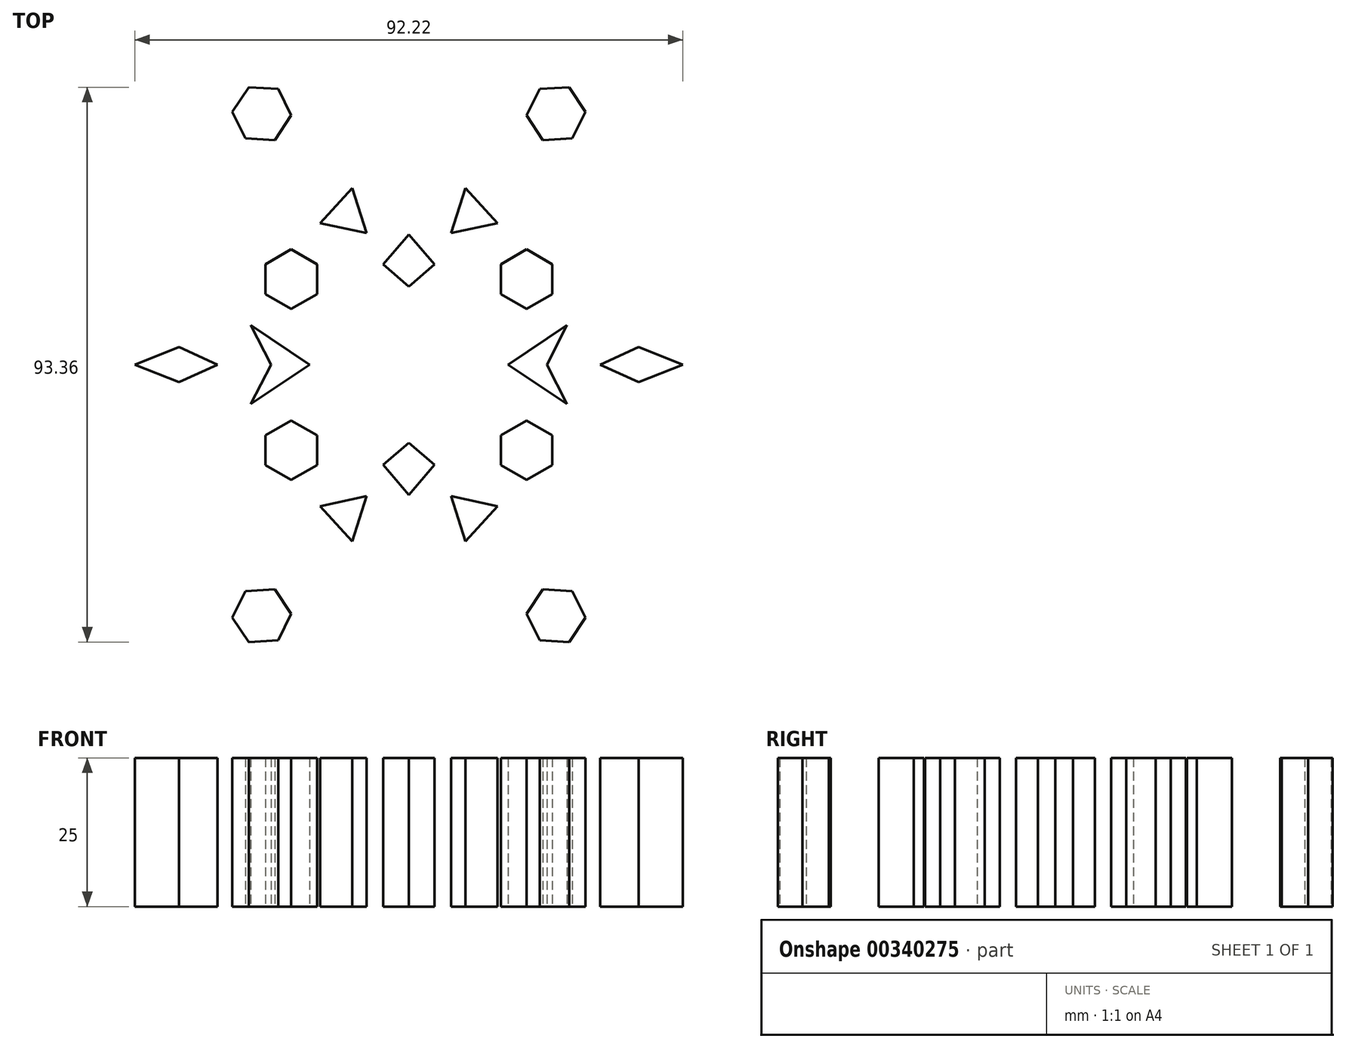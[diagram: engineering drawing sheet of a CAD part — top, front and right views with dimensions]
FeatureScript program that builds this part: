
annotation { "Feature Type Name" : "Feature", "Feature Type Description" : "" }
export const myFeature = defineFeature(function(context is Context, id is Id, definition is map)
    precondition{}
    {
        {
            var Q0;
            Q0=qCreatedBy(makeId("Top.planeOp"),FACE);
            var sketch = newSketch(context, id + "F0", { "sketchPlane" : qUnion([Q0])});
            skLineSegment(sketch, "E0.0", {"start": v(-31.3, 54.1) * mm, "end": v(31.2, 54.15) * mm});
            skLineSegment(sketch, "E0.1", {"start": v(31.2, 54.15) * mm, "end": v(62.5, 0.05) * mm});
            skLineSegment(sketch, "E0.2", {"start": v(62.5, 0.05) * mm, "end": v(31.3, -54.1) * mm});
            skLineSegment(sketch, "E0.3", {"start": v(31.3, -54.1) * mm, "end": v(-31.2, -54.15) * mm});
            skLineSegment(sketch, "E0.4", {"start": v(-31.2, -54.15) * mm, "end": v(-62.5, -0.05) * mm});
            skLineSegment(sketch, "E0.5", {"start": v(-62.5, -0.05) * mm, "end": v(-31.3, 54.1) * mm});
            skLineSegment(sketch, "E1.0", {"start": v(-37.55, 13.07) * mm, "end": v(-54.8, 12.82) * mm});
            skLineSegment(sketch, "E1.4", {"start": v(-39, 41.23) * mm, "end": v(-30.16, 26.43) * mm});
            skLineSegment(sketch, "E1.5", {"start": v(-30.16, 26.43) * mm, "end": v(-37.55, 13.07) * mm});
            skLineSegment(sketch, "E2.MirrorCS", {"start": v(39, 41.23) * mm, "end": v(30.16, 26.43) * mm});
            skLineSegment(sketch, "E3.MirrorCS", {"start": v(30.16, 26.43) * mm, "end": v(37.55, 13.07) * mm});
            skLineSegment(sketch, "E4.MirrorCS", {"start": v(37.55, 13.07) * mm, "end": v(54.8, 12.82) * mm});
            skLineSegment(sketch, "E5.MirrorCS", {"start": v(-37.55, -13.07) * mm, "end": v(-54.8, -12.82) * mm});
            skLineSegment(sketch, "E6.MirrorCS", {"start": v(-30.16, -26.43) * mm, "end": v(-37.55, -13.07) * mm});
            skLineSegment(sketch, "E7.MirrorCS", {"start": v(-39, -41.23) * mm, "end": v(-30.16, -26.43) * mm});
            skLineSegment(sketch, "E8.MirrorCS", {"start": v(39, -41.23) * mm, "end": v(30.16, -26.43) * mm});
            skLineSegment(sketch, "E9.MirrorCS", {"start": v(30.16, -26.43) * mm, "end": v(37.55, -13.07) * mm});
            skLineSegment(sketch, "E10.MirrorCS", {"start": v(37.55, -13.07) * mm, "end": v(54.8, -12.82) * mm});
            skLineSegment(sketch, "E11.0", {"start": v(-8.68, 41.12) * mm, "end": v(-16.3, 54.12) * mm});
            skLineSegment(sketch, "E11.4", {"start": v(16.2, 53.88) * mm, "end": v(6.98, 40.87) * mm});
            skLineSegment(sketch, "E11.5", {"start": v(6.98, 40.87) * mm, "end": v(-8.68, 41.12) * mm});
            skLineSegment(sketch, "E12.MirrorCS", {"start": v(-8.68, -41.12) * mm, "end": v(-16.3, -54.12) * mm});
            skLineSegment(sketch, "E13.MirrorCS", {"start": v(6.98, -40.87) * mm, "end": v(-8.68, -41.12) * mm});
            skLineSegment(sketch, "E14.MirrorCS", {"start": v(16.2, -53.88) * mm, "end": v(6.98, -40.87) * mm});
            skLineSegment(sketch, "E15.0", {"start": v(-7.43, 4.18) * mm, "end": v(-0.1, 8.52) * mm});
            skLineSegment(sketch, "E15.1", {"start": v(-0.1, 8.52) * mm, "end": v(7.33, 4.34) * mm});
            skLineSegment(sketch, "E15.2", {"start": v(7.33, 4.34) * mm, "end": v(7.43, -4.18) * mm});
            skLineSegment(sketch, "E15.3", {"start": v(7.43, -4.18) * mm, "end": v(0.1, -8.52) * mm});
            skLineSegment(sketch, "E15.4", {"start": v(0.1, -8.52) * mm, "end": v(-7.33, -4.34) * mm});
            skLineSegment(sketch, "E15.5", {"start": v(-7.33, -4.34) * mm, "end": v(-7.43, 4.18) * mm});
            skSolve(sketch);
        }
        {
            var Q0;
            {var subQ5=sQuery(id+"F0.wireOp",EDGE,"E0.3");Q0=makeQuery(id+"F0.imprint","IMPRINT",FACE,{"disambiguationData":[TD([[makeQuery(id+"F0.imprint","IMPRINT",EDGE,{"derivedFrom":subQ5}),-1.0]])]});}
            var sketch = newSketch(context, id + "F1", { "sketchPlane" : qUnion([Q0])});
            skLineSegment(sketch, "E16", {"start": v(-49.5, 13.15) * mm, "end": v(-41.77, 5.72) * mm});
            skLineSegment(sketch, "E17", {"start": v(-41.77, 5.72) * mm, "end": v(-45.64, 14.08) * mm});
            skPoint(sketch, "E17.endSnap0", {"position": v(-45.64, 9.44) * mm});
            skLineSegment(sketch, "E18", {"start": v(-37.75, 13.15) * mm, "end": v(-34.84, 6.87) * mm});
            skLineSegment(sketch, "E19", {"start": v(-34.84, 6.87) * mm, "end": v(-34.84, 18.41) * mm});
            skLineSegment(sketch, "E20", {"start": v(-34.84, 18.41) * mm, "end": v(-26, 23.36) * mm});
            skLineSegment(sketch, "E21", {"start": v(-26, 23.36) * mm, "end": v(-31.25, 26.77) * mm});
            skLineSegment(sketch, "E22", {"start": v(-58.8, 6.34) * mm, "end": v(-52.3, 3.25) * mm});
            skLineSegment(sketch, "E23", {"start": v(-52.3, 3.25) * mm, "end": v(-56.94, 10.06) * mm});
            skLineSegment(sketch, "E24", {"start": v(-31.25, 26.77) * mm, "end": v(-23.2, 26.77) * mm});
            skLineSegment(sketch, "E25", {"start": v(-23.2, 26.77) * mm, "end": v(-34.66, 32.95) * mm});
            skLineSegment(sketch, "E26", {"start": v(-12.07, 46.57) * mm, "end": v(-12.07, 32.95) * mm});
            skLineSegment(sketch, "E27", {"start": v(-12.07, 32.95) * mm, "end": v(-8.66, 39.76) * mm});
            skPoint(sketch, "E27.endSnap0", {"position": v(-12.07, 39.76) * mm});
            skLineSegment(sketch, "E28", {"start": v(-8.66, 39.76) * mm, "end": v(0, 35.43) * mm});
            skCircle(sketch, "E29.cCircle", {"center": v(-24.75, 42.24) * mm, "radius": 4.96 * mm, "construction": true});
            skLineSegment(sketch, "E29.0", {"start": v(-19.8, 41.93) * mm, "end": v(-22.55, 37.8) * mm});
            skLineSegment(sketch, "E29.1", {"start": v(-22.55, 37.8) * mm, "end": v(-27.5, 38.1) * mm});
            skLineSegment(sketch, "E29.2", {"start": v(-27.5, 38.1) * mm, "end": v(-29.7, 42.55) * mm});
            skLineSegment(sketch, "E29.3", {"start": v(-29.7, 42.55) * mm, "end": v(-26.96, 46.68) * mm});
            skLineSegment(sketch, "E29.4", {"start": v(-26.96, 46.68) * mm, "end": v(-22.01, 46.37) * mm});
            skLineSegment(sketch, "E29.5", {"start": v(-22.01, 46.37) * mm, "end": v(-19.8, 41.93) * mm});
            skLineSegment(sketch, "E30.MirrorCS", {"start": v(8.66, 39.76) * mm, "end": v(0, 35.43) * mm});
            skLineSegment(sketch, "E31.MirrorCS", {"start": v(12.07, 32.95) * mm, "end": v(8.66, 39.76) * mm});
            skPoint(sketch, "E32.MirrorP", {"position": v(12.07, 39.76) * mm});
            skLineSegment(sketch, "E33.MirrorCS", {"start": v(12.07, 46.57) * mm, "end": v(12.07, 32.95) * mm});
            skLineSegment(sketch, "E34.MirrorCS", {"start": v(23.2, 26.77) * mm, "end": v(34.66, 32.95) * mm});
            skLineSegment(sketch, "E35.MirrorCS", {"start": v(31.25, 26.77) * mm, "end": v(23.2, 26.77) * mm});
            skLineSegment(sketch, "E36.MirrorCS", {"start": v(34.84, 18.41) * mm, "end": v(26, 23.36) * mm});
            skLineSegment(sketch, "E37.MirrorCS", {"start": v(26, 23.36) * mm, "end": v(31.25, 26.77) * mm});
            skLineSegment(sketch, "E38.MirrorCS", {"start": v(34.84, 6.87) * mm, "end": v(34.84, 18.41) * mm});
            skPoint(sketch, "E39.MirrorP", {"position": v(45.64, 9.44) * mm});
            skLineSegment(sketch, "E40.MirrorCS", {"start": v(37.75, 13.15) * mm, "end": v(34.84, 6.87) * mm});
            skLineSegment(sketch, "E41.MirrorCS", {"start": v(41.77, 5.72) * mm, "end": v(45.64, 14.08) * mm});
            skLineSegment(sketch, "E42.MirrorCS", {"start": v(49.5, 13.15) * mm, "end": v(41.77, 5.72) * mm});
            skLineSegment(sketch, "E43.MirrorCS", {"start": v(58.8, 6.34) * mm, "end": v(52.3, 3.25) * mm});
            skLineSegment(sketch, "E44.MirrorCS", {"start": v(52.3, 3.25) * mm, "end": v(56.94, 10.06) * mm});
            skLineSegment(sketch, "E45.MirrorCS", {"start": v(41.77, -5.72) * mm, "end": v(45.64, -14.08) * mm});
            skLineSegment(sketch, "E46.MirrorCS", {"start": v(49.5, -13.15) * mm, "end": v(41.77, -5.72) * mm});
            skPoint(sketch, "E47.MirrorP", {"position": v(45.64, -9.44) * mm});
            skLineSegment(sketch, "E48.MirrorCS", {"start": v(-22.55, -37.8) * mm, "end": v(-27.5, -38.1) * mm});
            skLineSegment(sketch, "E49.MirrorCS", {"start": v(-22.01, -46.37) * mm, "end": v(-19.8, -41.93) * mm});
            skLineSegment(sketch, "E50.MirrorCS", {"start": v(26, -23.36) * mm, "end": v(31.25, -26.77) * mm});
            skCircle(sketch, "E51.MirrorC", {"center": v(-24.75, -42.24) * mm, "radius": 4.96 * mm, "construction": true});
            skLineSegment(sketch, "E52.MirrorCS", {"start": v(37.75, -13.15) * mm, "end": v(34.84, -6.87) * mm});
            skLineSegment(sketch, "E53.MirrorCS", {"start": v(-19.8, -41.93) * mm, "end": v(-22.55, -37.8) * mm});
            skLineSegment(sketch, "E54.MirrorCS", {"start": v(-12.07, -32.95) * mm, "end": v(-8.66, -39.76) * mm});
            skLineSegment(sketch, "E55.MirrorCS", {"start": v(31.25, -26.77) * mm, "end": v(23.2, -26.77) * mm});
            skLineSegment(sketch, "E56.MirrorCS", {"start": v(-26.96, -46.68) * mm, "end": v(-22.01, -46.37) * mm});
            skLineSegment(sketch, "E57.MirrorCS", {"start": v(-27.5, -38.1) * mm, "end": v(-29.7, -42.55) * mm});
            skLineSegment(sketch, "E58.MirrorCS", {"start": v(-31.25, -26.77) * mm, "end": v(-23.2, -26.77) * mm});
            skLineSegment(sketch, "E59.MirrorCS", {"start": v(-29.7, -42.55) * mm, "end": v(-26.96, -46.68) * mm});
            skLineSegment(sketch, "E60.MirrorCS", {"start": v(12.07, -32.95) * mm, "end": v(8.66, -39.76) * mm});
            skLineSegment(sketch, "E61.MirrorCS", {"start": v(-26, -23.36) * mm, "end": v(-31.25, -26.77) * mm});
            skLineSegment(sketch, "E62.MirrorCS", {"start": v(-37.75, -13.15) * mm, "end": v(-34.84, -6.87) * mm});
            skLineSegment(sketch, "E63.MirrorCS", {"start": v(34.84, -6.87) * mm, "end": v(34.84, -18.41) * mm});
            skLineSegment(sketch, "E64.MirrorCS", {"start": v(-49.5, -13.15) * mm, "end": v(-41.77, -5.72) * mm});
            skLineSegment(sketch, "E65.MirrorCS", {"start": v(-58.8, -6.34) * mm, "end": v(-52.3, -3.25) * mm});
            skLineSegment(sketch, "E66.MirrorCS", {"start": v(12.07, -46.57) * mm, "end": v(12.07, -32.95) * mm});
            skLineSegment(sketch, "E67.MirrorCS", {"start": v(-41.77, -5.72) * mm, "end": v(-45.64, -14.08) * mm});
            skLineSegment(sketch, "E68.MirrorCS", {"start": v(52.3, -3.25) * mm, "end": v(56.94, -10.06) * mm});
            skLineSegment(sketch, "E69.MirrorCS", {"start": v(58.8, -6.34) * mm, "end": v(52.3, -3.25) * mm});
            skLineSegment(sketch, "E70.MirrorCS", {"start": v(-52.3, -3.25) * mm, "end": v(-56.94, -10.06) * mm});
            skLineSegment(sketch, "E71.MirrorCS", {"start": v(-12.07, -46.57) * mm, "end": v(-12.07, -32.95) * mm});
            skLineSegment(sketch, "E72.MirrorCS", {"start": v(23.2, -26.77) * mm, "end": v(34.66, -32.95) * mm});
            skPoint(sketch, "E73.MirrorP", {"position": v(-45.64, -9.44) * mm});
            skPoint(sketch, "E74.MirrorP", {"position": v(-12.07, -39.76) * mm});
            skPoint(sketch, "E75.MirrorP", {"position": v(12.07, -39.76) * mm});
            skLineSegment(sketch, "E76.MirrorCS", {"start": v(-23.2, -26.77) * mm, "end": v(-34.66, -32.95) * mm});
            skLineSegment(sketch, "E77.MirrorCS", {"start": v(34.84, -18.41) * mm, "end": v(26, -23.36) * mm});
            skLineSegment(sketch, "E78.MirrorCS", {"start": v(-8.66, -39.76) * mm, "end": v(0, -35.43) * mm});
            skLineSegment(sketch, "E79.MirrorCS", {"start": v(-34.84, -18.41) * mm, "end": v(-26, -23.36) * mm});
            skLineSegment(sketch, "E80.MirrorCS", {"start": v(8.66, -39.76) * mm, "end": v(0, -35.43) * mm});
            skLineSegment(sketch, "E81.MirrorCS", {"start": v(-34.84, -6.87) * mm, "end": v(-34.84, -18.41) * mm});
            skLineSegment(sketch, "E82.MirrorCS", {"start": v(22.55, 37.8) * mm, "end": v(27.5, 38.1) * mm});
            skLineSegment(sketch, "E83.MirrorCS", {"start": v(19.8, 41.93) * mm, "end": v(22.55, 37.8) * mm});
            skCircle(sketch, "E84.MirrorC", {"center": v(24.75, 42.24) * mm, "radius": 4.96 * mm, "construction": true});
            skLineSegment(sketch, "E85.MirrorCS", {"start": v(29.7, 42.55) * mm, "end": v(26.96, 46.68) * mm});
            skLineSegment(sketch, "E86.MirrorCS", {"start": v(27.5, 38.1) * mm, "end": v(29.7, 42.55) * mm});
            skLineSegment(sketch, "E87.MirrorCS", {"start": v(26.96, 46.68) * mm, "end": v(22.01, 46.37) * mm});
            skLineSegment(sketch, "E88.MirrorCS", {"start": v(22.01, 46.37) * mm, "end": v(19.8, 41.93) * mm});
            skLineSegment(sketch, "E89.MirrorCS", {"start": v(22.55, -37.8) * mm, "end": v(27.5, -38.1) * mm});
            skLineSegment(sketch, "E90.MirrorCS", {"start": v(19.8, -41.93) * mm, "end": v(22.55, -37.8) * mm});
            skCircle(sketch, "E91.MirrorC", {"center": v(24.75, -42.24) * mm, "radius": 4.96 * mm, "construction": true});
            skLineSegment(sketch, "E92.MirrorCS", {"start": v(29.7, -42.55) * mm, "end": v(26.96, -46.68) * mm});
            skLineSegment(sketch, "E93.MirrorCS", {"start": v(27.5, -38.1) * mm, "end": v(29.7, -42.55) * mm});
            skLineSegment(sketch, "E94.MirrorCS", {"start": v(22.01, -46.37) * mm, "end": v(19.8, -41.93) * mm});
            skLineSegment(sketch, "E95.MirrorCS", {"start": v(26.96, -46.68) * mm, "end": v(22.01, -46.37) * mm});
            skCircle(sketch, "E96.cCircle", {"center": v(-19.8, 14.39) * mm, "radius": 4.33 * mm, "construction": true});
            skLineSegment(sketch, "E96.0", {"start": v(-15.47, 16.89) * mm, "end": v(-15.47, 11.89) * mm});
            skLineSegment(sketch, "E96.1", {"start": v(-15.47, 11.89) * mm, "end": v(-19.8, 9.39) * mm});
            skLineSegment(sketch, "E96.2", {"start": v(-19.8, 9.39) * mm, "end": v(-24.14, 11.89) * mm});
            skLineSegment(sketch, "E96.3", {"start": v(-24.14, 11.89) * mm, "end": v(-24.14, 16.89) * mm});
            skLineSegment(sketch, "E96.4", {"start": v(-24.14, 16.89) * mm, "end": v(-19.8, 19.4) * mm});
            skLineSegment(sketch, "E96.5", {"start": v(-19.8, 19.4) * mm, "end": v(-15.47, 16.89) * mm});
            skPoint(sketch, "E96.0.midPoint", {"position": v(-15.47, 14.39) * mm});
            skLineSegment(sketch, "E97.0", {"start": v(-7.12, 22.12) * mm, "end": v(-14.9, 23.82) * mm});
            skLineSegment(sketch, "E97.1", {"start": v(-14.9, 23.82) * mm, "end": v(-9.54, 29.71) * mm});
            skLineSegment(sketch, "E97.2", {"start": v(-9.54, 29.71) * mm, "end": v(-7.12, 22.12) * mm});
            skLineSegment(sketch, "E98.MirrorCS", {"start": v(7.12, 22.12) * mm, "end": v(14.9, 23.82) * mm});
            skLineSegment(sketch, "E99.MirrorCS", {"start": v(14.9, 23.82) * mm, "end": v(9.54, 29.71) * mm});
            skLineSegment(sketch, "E100.MirrorCS", {"start": v(9.54, 29.71) * mm, "end": v(7.12, 22.12) * mm});
            skLineSegment(sketch, "E101.MirrorCS", {"start": v(19.8, 9.39) * mm, "end": v(24.14, 11.89) * mm});
            skPoint(sketch, "E102.MirrorP", {"position": v(15.47, 14.39) * mm});
            skLineSegment(sketch, "E103.MirrorCS", {"start": v(24.14, 11.89) * mm, "end": v(24.14, 16.89) * mm});
            skLineSegment(sketch, "E104.MirrorCS", {"start": v(15.47, 11.89) * mm, "end": v(19.8, 9.39) * mm});
            skLineSegment(sketch, "E105.MirrorCS", {"start": v(19.8, 19.4) * mm, "end": v(15.47, 16.89) * mm});
            skCircle(sketch, "E106.MirrorC", {"center": v(19.8, 14.39) * mm, "radius": 4.33 * mm, "construction": true});
            skLineSegment(sketch, "E107.MirrorCS", {"start": v(24.14, 16.89) * mm, "end": v(19.8, 19.4) * mm});
            skLineSegment(sketch, "E108.MirrorCS", {"start": v(15.47, 16.89) * mm, "end": v(15.47, 11.89) * mm});
            skLineSegment(sketch, "E109.MirrorCS", {"start": v(7.12, -22.12) * mm, "end": v(14.9, -23.82) * mm});
            skLineSegment(sketch, "E110.MirrorCS", {"start": v(14.9, -23.82) * mm, "end": v(9.54, -29.71) * mm});
            skLineSegment(sketch, "E111.MirrorCS", {"start": v(-9.54, -29.71) * mm, "end": v(-7.12, -22.12) * mm});
            skLineSegment(sketch, "E112.MirrorCS", {"start": v(9.54, -29.71) * mm, "end": v(7.12, -22.12) * mm});
            skLineSegment(sketch, "E113.MirrorCS", {"start": v(-14.9, -23.82) * mm, "end": v(-9.54, -29.71) * mm});
            skPoint(sketch, "E114.MirrorP", {"position": v(15.47, -14.39) * mm});
            skPoint(sketch, "E115.MirrorP", {"position": v(-15.47, -14.39) * mm});
            skLineSegment(sketch, "E116.MirrorCS", {"start": v(-19.8, -19.4) * mm, "end": v(-15.47, -16.89) * mm});
            skLineSegment(sketch, "E117.MirrorCS", {"start": v(19.8, -19.4) * mm, "end": v(15.47, -16.89) * mm});
            skLineSegment(sketch, "E118.MirrorCS", {"start": v(-7.12, -22.12) * mm, "end": v(-14.9, -23.82) * mm});
            skLineSegment(sketch, "E119.MirrorCS", {"start": v(-19.8, -9.39) * mm, "end": v(-24.14, -11.89) * mm});
            skLineSegment(sketch, "E120.MirrorCS", {"start": v(-24.14, -11.89) * mm, "end": v(-24.14, -16.89) * mm});
            skLineSegment(sketch, "E121.MirrorCS", {"start": v(-15.47, -11.89) * mm, "end": v(-19.8, -9.39) * mm});
            skLineSegment(sketch, "E122.MirrorCS", {"start": v(-15.47, -16.89) * mm, "end": v(-15.47, -11.89) * mm});
            skCircle(sketch, "E123.MirrorC", {"center": v(-19.8, -14.39) * mm, "radius": 4.33 * mm, "construction": true});
            skLineSegment(sketch, "E124.MirrorCS", {"start": v(-24.14, -16.89) * mm, "end": v(-19.8, -19.4) * mm});
            skLineSegment(sketch, "E125.MirrorCS", {"start": v(24.14, -16.89) * mm, "end": v(19.8, -19.4) * mm});
            skLineSegment(sketch, "E126.MirrorCS", {"start": v(15.47, -16.89) * mm, "end": v(15.47, -11.89) * mm});
            skCircle(sketch, "E127.MirrorC", {"center": v(19.8, -14.39) * mm, "radius": 4.33 * mm, "construction": true});
            skLineSegment(sketch, "E128.MirrorCS", {"start": v(24.14, -11.89) * mm, "end": v(24.14, -16.89) * mm});
            skLineSegment(sketch, "E129.MirrorCS", {"start": v(19.8, -9.39) * mm, "end": v(24.14, -11.89) * mm});
            skLineSegment(sketch, "E130.MirrorCS", {"start": v(15.47, -11.89) * mm, "end": v(19.8, -9.39) * mm});
            skLineSegment(sketch, "E131", {"start": v(-16.7, 0) * mm, "end": v(-26.61, 6.65) * mm});
            skLineSegment(sketch, "E132", {"start": v(-26.61, 6.65) * mm, "end": v(-23.2, 0) * mm});
            skLineSegment(sketch, "E133", {"start": v(0, 13.15) * mm, "end": v(-4.33, 16.86) * mm});
            skLineSegment(sketch, "E134", {"start": v(-4.33, 16.86) * mm, "end": v(0.18, 22.12) * mm});
            skLineSegment(sketch, "E135.MirrorCS", {"start": v(-26.61, -6.65) * mm, "end": v(-23.2, 0) * mm});
            skLineSegment(sketch, "E136.MirrorCS", {"start": v(-16.7, 0) * mm, "end": v(-26.61, -6.65) * mm});
            skLineSegment(sketch, "E137.MirrorCS", {"start": v(-4.33, -16.86) * mm, "end": v(0.18, -22.12) * mm});
            skLineSegment(sketch, "E138.MirrorCS", {"start": v(0, -13.15) * mm, "end": v(-4.33, -16.86) * mm});
            skLineSegment(sketch, "E139.MirrorCS", {"start": v(4.33, 16.86) * mm, "end": v(-0.18, 22.12) * mm});
            skLineSegment(sketch, "E140.MirrorCS", {"start": v(0, 13.15) * mm, "end": v(4.33, 16.86) * mm});
            skLineSegment(sketch, "E141.MirrorCS", {"start": v(0, -13.15) * mm, "end": v(4.33, -16.86) * mm});
            skLineSegment(sketch, "E142.MirrorCS", {"start": v(4.33, -16.86) * mm, "end": v(-0.18, -22.12) * mm});
            skLineSegment(sketch, "E143.MirrorCS", {"start": v(16.7, 0) * mm, "end": v(26.61, 6.65) * mm});
            skLineSegment(sketch, "E144.MirrorCS", {"start": v(26.61, 6.65) * mm, "end": v(23.2, 0) * mm});
            skLineSegment(sketch, "E145.MirrorCS", {"start": v(16.7, 0) * mm, "end": v(26.61, -6.65) * mm});
            skLineSegment(sketch, "E146.MirrorCS", {"start": v(26.61, -6.65) * mm, "end": v(23.2, 0) * mm});
            skLineSegment(sketch, "E147", {"start": v(-37.13, 43.17) * mm, "end": v(-34.66, 43.17) * mm});
            skLineSegment(sketch, "E148", {"start": v(-34.66, 43.17) * mm, "end": v(-34.66, 47.5) * mm});
            skLineSegment(sketch, "E149", {"start": v(-23.83, 54) * mm, "end": v(-20.42, 51.21) * mm});
            skLineSegment(sketch, "E150", {"start": v(-20.42, 51.21) * mm, "end": v(-18.19, 53.94) * mm});
            skLineSegment(sketch, "E151", {"start": v(-46.1, 0) * mm, "end": v(-38.68, 2.94) * mm});
            skLineSegment(sketch, "E152", {"start": v(-38.68, 2.94) * mm, "end": v(-32.18, 0) * mm});
            skLineSegment(sketch, "E153.MirrorCS", {"start": v(34.66, 43.17) * mm, "end": v(34.66, 47.5) * mm});
            skLineSegment(sketch, "E154.MirrorCS", {"start": v(20.42, 51.21) * mm, "end": v(18.19, 53.94) * mm});
            skLineSegment(sketch, "E155.MirrorCS", {"start": v(23.83, 54) * mm, "end": v(20.42, 51.21) * mm});
            skLineSegment(sketch, "E156.MirrorCS", {"start": v(37.13, 43.17) * mm, "end": v(34.66, 43.17) * mm});
            skLineSegment(sketch, "E157.MirrorCS", {"start": v(-46.1, 0) * mm, "end": v(-38.68, -2.94) * mm});
            skLineSegment(sketch, "E158.MirrorCS", {"start": v(-38.68, -2.94) * mm, "end": v(-32.18, 0) * mm});
            skLineSegment(sketch, "E159.MirrorCS", {"start": v(37.13, -43.17) * mm, "end": v(34.66, -43.17) * mm});
            skLineSegment(sketch, "E160.MirrorCS", {"start": v(-20.42, -51.21) * mm, "end": v(-18.19, -53.94) * mm});
            skLineSegment(sketch, "E161.MirrorCS", {"start": v(-23.83, -54) * mm, "end": v(-20.42, -51.21) * mm});
            skLineSegment(sketch, "E162.MirrorCS", {"start": v(20.42, -51.21) * mm, "end": v(18.19, -53.94) * mm});
            skLineSegment(sketch, "E163.MirrorCS", {"start": v(23.83, -54) * mm, "end": v(20.42, -51.21) * mm});
            skLineSegment(sketch, "E164.MirrorCS", {"start": v(-37.13, -43.17) * mm, "end": v(-34.66, -43.17) * mm});
            skLineSegment(sketch, "E165.MirrorCS", {"start": v(34.66, -43.17) * mm, "end": v(34.66, -47.5) * mm});
            skLineSegment(sketch, "E166.MirrorCS", {"start": v(-34.66, -43.17) * mm, "end": v(-34.66, -47.5) * mm});
            skLineSegment(sketch, "E167.MirrorCS", {"start": v(38.68, 2.94) * mm, "end": v(32.18, 0) * mm});
            skLineSegment(sketch, "E168.MirrorCS", {"start": v(46.1, 0) * mm, "end": v(38.68, -2.94) * mm});
            skLineSegment(sketch, "E169.MirrorCS", {"start": v(46.1, 0) * mm, "end": v(38.68, 2.94) * mm});
            skLineSegment(sketch, "E170.MirrorCS", {"start": v(38.68, -2.94) * mm, "end": v(32.18, 0) * mm});
            skSolve(sketch);
        }
        {
            var Q0;
            Q0 = qSketchRegion(id + "F1", true);
            extrude(context, id + "F2", {"entities" : qUnion([Q0]), "depth" : 25 * mm});
        }
    });
